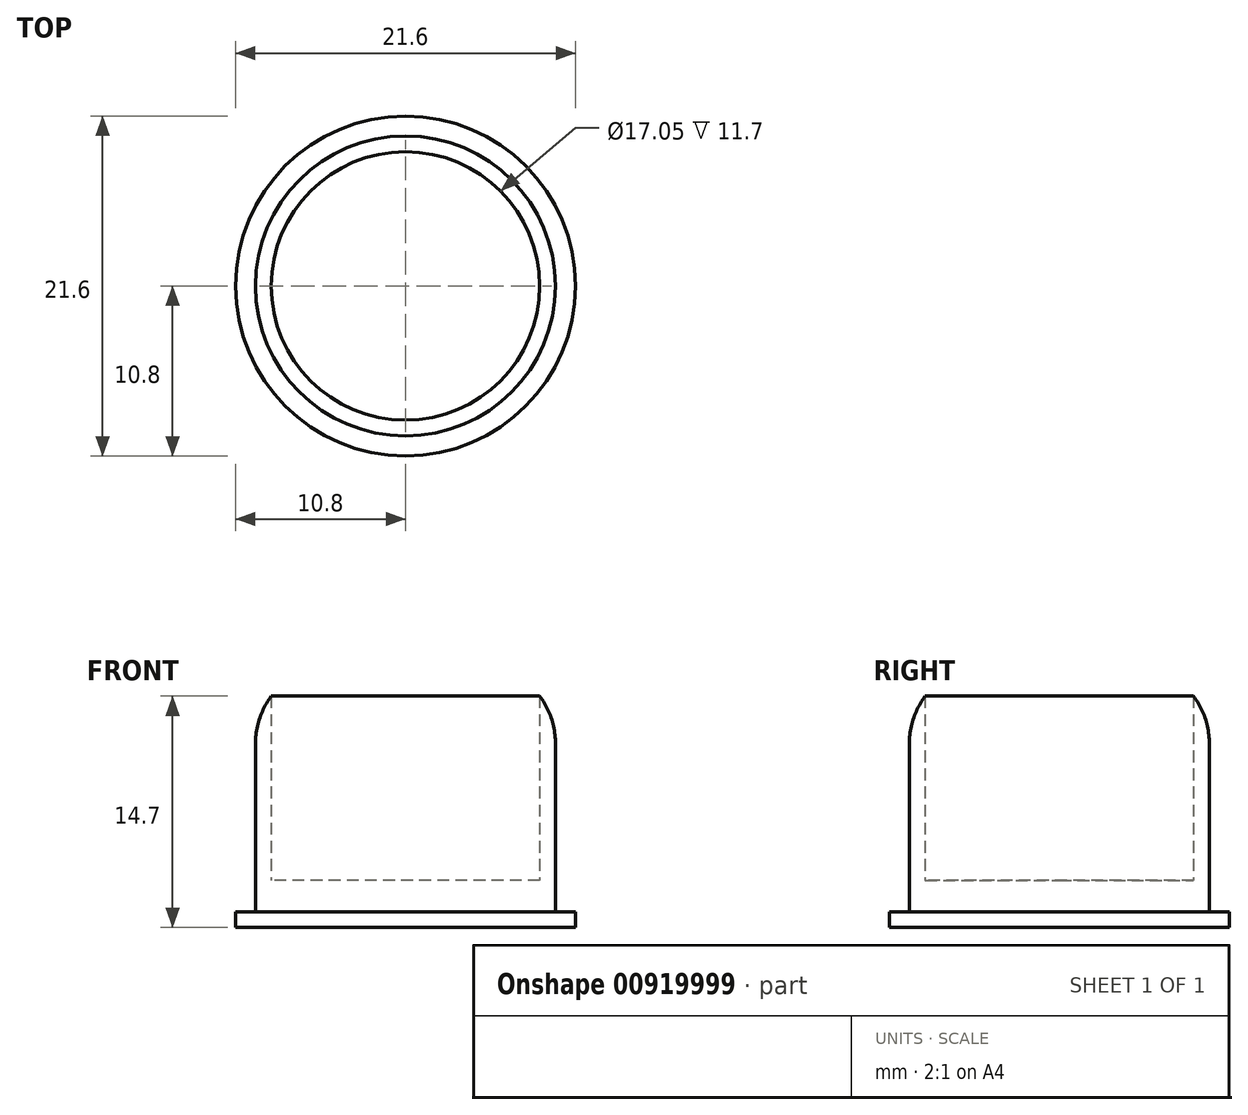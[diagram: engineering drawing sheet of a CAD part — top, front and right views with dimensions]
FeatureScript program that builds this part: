
annotation { "Feature Type Name" : "Feature", "Feature Type Description" : "" }
export const myFeature = defineFeature(function(context is Context, id is Id, definition is map)
    precondition{}
    {
        {
            var Q0;
            Q0=qCreatedBy(makeId("Top.planeOp"),FACE);
            var sketch = newSketch(context, id + "F0", { "sketchPlane" : qUnion([Q0])});
            skCircle(sketch, "E0", {"center": v(0, 0) * mm, "radius": 9.52 * mm});
            skSolve(sketch);
        }
        {
            var Q0;
            Q0=makeQuery(id+"F0.imprint","IMPRINT",FACE,{"disambiguationData":[TD([[makeQuery(id+"F0.imprint","IMPRINT",EDGE,{"derivedFrom":sQuery(id+"F0.wireOp",EDGE,"E0")}),1.0]])]});
            extrude(context, id + "F1", {"entities" : qUnion([Q0]), "depth" : 12.7 * mm, "offsetDistance" : 25.4 * mm});
        }
        {
            var Q0;
            Q0=makeQuery(id+"F1.opExtrude","CAP_FACE",FACE,{"disambiguationData":[OSD([sQuery(id+"F0.wireOp",EDGE,"E0")])],"isStart":false});
            shell(context, id + "F2", {"entities" : qUnion([Q0]), "thickness" : 1 * mm});
        }
        {
            var Q0;
            Q0=makeQuery(id+"F1.opExtrude","CAP_FACE",FACE,{"disambiguationData":[OSD([sQuery(id+"F0.wireOp",EDGE,"E0")])],"isStart":true});
            extrude(context, id + "F3", {"entities" : qUnion([Q0]), "operationType" : NewBodyOperationType.ADD, "depth" : 1 * mm, "offsetDistance" : 25.4 * mm});
        }
        {
            var Q0;
            Q0=makeQuery(id+"F3.opExtrude","CAP_FACE",FACE,{"disambiguationData":[OSD([sQuery(id+"F0.wireOp",EDGE,"E0")])],"isStart":false});
            var sketch = newSketch(context, id + "F4", { "sketchPlane" : qUnion([Q0])});
            skCircle(sketch, "E1", {"center": v(0, 0) * mm, "radius": 10.8 * mm});
            skSolve(sketch);
        }
        {
            var Q0;
            Q0=makeQuery(id+"F4.imprint","IMPRINT",FACE,{"disambiguationData":[TD([[makeQuery(id+"F4.imprint","IMPRINT",EDGE,{"derivedFrom":sQuery(id+"F4.wireOp",EDGE,"E1")}),1.0]])]});
            var Q1;
            Q1=makeQuery(id+"F4.imprint","IMPRINT",FACE,{"disambiguationData":[TD([[makeQuery(id+"F4.imprint","IMPRINT",EDGE,{"derivedFrom":makeQuery(id+"F3.opExtrude","CAP_EDGE",EDGE,{"disambiguationData":[OSD([sQuery(id+"F0.wireOp",EDGE,"E0")])],"isStart":false})}),-1.0]])]});
            extrude(context, id + "F5", {"entities" : qUnion([Q0, Q1]), "depth" : 1 * mm, "offsetDistance" : 25.4 * mm});
        }
        {
            var Q0;
            Q0=makeQuery(id+"F1.opExtrude","CAP_EDGE",EDGE,{"disambiguationData":[OSD([sQuery(id+"F0.wireOp",EDGE,"E0")])],"isStart":false});
            fillet(context, id + "F6", {"entities" : qUnion([Q0]), "radius" : 5.08 * mm, "tangentPropagation" : true, "allowEdgeOverflow" : false});
        }
    });
